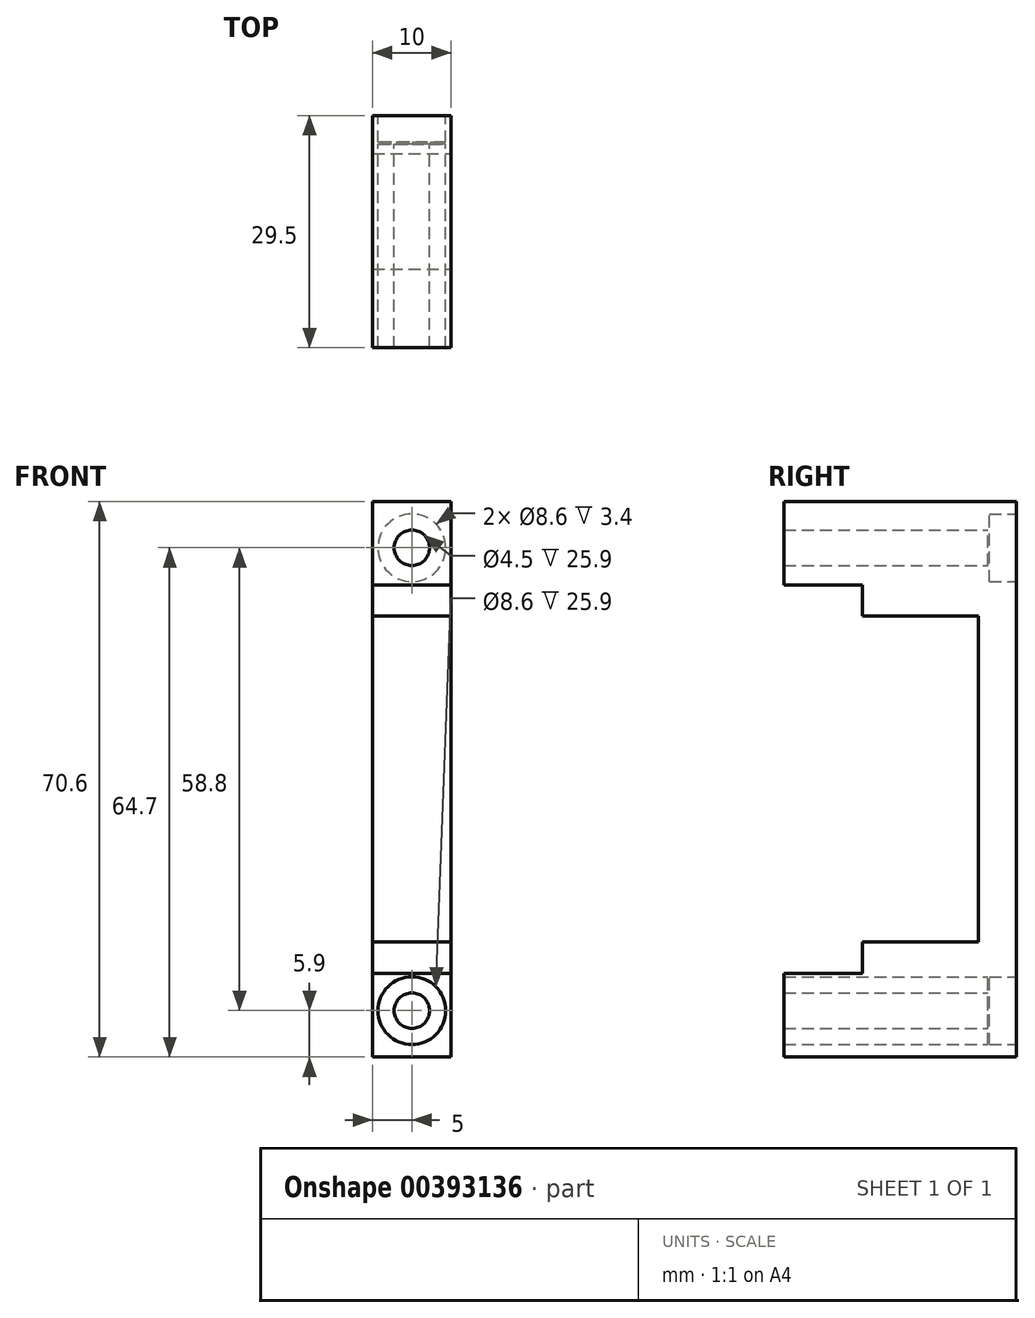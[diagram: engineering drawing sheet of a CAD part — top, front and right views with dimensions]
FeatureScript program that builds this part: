
annotation { "Feature Type Name" : "Feature", "Feature Type Description" : "" }
export const myFeature = defineFeature(function(context is Context, id is Id, definition is map)
    precondition{}
    {
        {
            var Q0;
            Q0=qCreatedBy(makeId("Front.planeOp"),FACE);
            var sketch = newSketch(context, id + "F0", { "sketchPlane" : qUnion([Q0])});
            skLineSegment(sketch, "E0", {"start": v(5, 35.3) * mm, "end": v(-5, 35.3) * mm});
            skPoint(sketch, "E1", {"position": v(0, 35.3) * mm});
            skLineSegment(sketch, "E2.MirrorCS", {"start": v(5, -35.3) * mm, "end": v(-5, -35.3) * mm});
            skPoint(sketch, "E3.MirrorP", {"position": v(0, -35.3) * mm});
            skLineSegment(sketch, "E4", {"start": v(-5, 35.3) * mm, "end": v(-5, -35.3) * mm});
            skLineSegment(sketch, "E5", {"start": v(5, -35.3) * mm, "end": v(5, 35.3) * mm});
            skLineSegment(sketch, "E6", {"start": v(-5, 24.7) * mm, "end": v(5, 24.7) * mm});
            skLineSegment(sketch, "E7", {"start": v(-5, 20.7) * mm, "end": v(5, 20.7) * mm});
            skLineSegment(sketch, "E8.MirrorCS", {"start": v(-5, -24.7) * mm, "end": v(5, -24.7) * mm});
            skLineSegment(sketch, "E9.MirrorCS", {"start": v(-5, -20.7) * mm, "end": v(5, -20.7) * mm});
            skCircle(sketch, "E10", {"center": v(0, 29.4) * mm, "radius": 2.25 * mm});
            skCircle(sketch, "E11", {"center": v(0, 29.4) * mm, "radius": 4.3 * mm});
            skCircle(sketch, "E12.MirrorC", {"center": v(0, -29.4) * mm, "radius": 2.25 * mm});
            skCircle(sketch, "E13.MirrorC", {"center": v(0, -29.4) * mm, "radius": 4.3 * mm});
            skSolve(sketch);
        }
        {
            var Q0;
            {var subQ0=sQuery(id+"F0.wireOp",EDGE,"E7");Q0=makeQuery(id+"F0.imprint","IMPRINT",FACE,{"disambiguationData":[TD([[makeQuery(id+"F0.imprint","IMPRINT",EDGE,{"derivedFrom":subQ0}),-1.0]])]});}
            extrude(context, id + "F1", {"entities" : qUnion([Q0]), "depth" : 4.8 * mm});
        }
        {
            var Q0;
            {var subQ0=sQuery(id+"F0.wireOp",EDGE,"E6");Q0=makeQuery(id+"F0.imprint","IMPRINT",FACE,{"disambiguationData":[TD([[makeQuery(id+"F0.imprint","IMPRINT",EDGE,{"derivedFrom":subQ0}),-1.0]])]});}
            var Q1;
            {var subQ0=sQuery(id+"F0.wireOp",EDGE,"E8.MirrorCS");Q1=makeQuery(id+"F0.imprint","IMPRINT",FACE,{"disambiguationData":[TD([[makeQuery(id+"F0.imprint","IMPRINT",EDGE,{"derivedFrom":subQ0}),1.0]])]});}
            extrude(context, id + "F2", {"entities" : qUnion([Q0, Q1]), "operationType" : NewBodyOperationType.ADD, "depth" : 19.5 * mm});
        }
        {
            var Q0;
            {var subQ1=sQuery(id+"F0.wireOp",EDGE,"E0");Q0=makeQuery(id+"F0.imprint","IMPRINT",FACE,{"disambiguationData":[TD([[makeQuery(id+"F0.imprint","IMPRINT",EDGE,{"derivedFrom":subQ1}),1.0]])]});}
            var Q1;
            Q1=makeQuery(id+"F0.imprint","IMPRINT",FACE,{"disambiguationData":[TD([[makeQuery(id+"F0.imprint","IMPRINT",EDGE,{"derivedFrom":sQuery(id+"F0.wireOp",EDGE,"E10")}),-1.0]])]});
            var Q2;
            {var subQ2=sQuery(id+"F0.wireOp",EDGE,"E2.MirrorCS");Q2=makeQuery(id+"F0.imprint","IMPRINT",FACE,{"disambiguationData":[TD([[makeQuery(id+"F0.imprint","IMPRINT",EDGE,{"derivedFrom":subQ2}),-1.0]])]});}
            var Q3;
            Q3=makeQuery(id+"F0.imprint","IMPRINT",FACE,{"disambiguationData":[TD([[makeQuery(id+"F0.imprint","IMPRINT",EDGE,{"derivedFrom":sQuery(id+"F0.wireOp",EDGE,"E12.MirrorC")}),1.0]])]});
            extrude(context, id + "F3", {"entities" : qUnion([Q0, Q1, Q2, Q3]), "operationType" : NewBodyOperationType.ADD, "depth" : 29.5 * mm});
        }
        {
            var Q0;
            Q0=makeQuery(id+"F0.imprint","IMPRINT",FACE,{"disambiguationData":[TD([[makeQuery(id+"F0.imprint","IMPRINT",EDGE,{"derivedFrom":sQuery(id+"F0.wireOp",EDGE,"E12.MirrorC")}),1.0]])]});
            var Q1;
            Q1=makeQuery(id+"F0.imprint","IMPRINT",FACE,{"disambiguationData":[TD([[makeQuery(id+"F0.imprint","IMPRINT",EDGE,{"derivedFrom":sQuery(id+"F0.wireOp",EDGE,"E10")}),-1.0]])]});
            extrude(context, id + "F4", {"entities" : qUnion([Q0, Q1]), "operationType" : NewBodyOperationType.REMOVE, "depth" : 3.4 * mm});
        }
        {
            var Q0;
            Q0=makeQuery(id+"F0.imprint","IMPRINT",FACE,{"disambiguationData":[TD([[makeQuery(id+"F0.imprint","IMPRINT",EDGE,{"derivedFrom":sQuery(id+"F0.wireOp",EDGE,"E10")}),1.0]])]});
            var Q1;
            Q1=makeQuery(id+"F0.imprint","IMPRINT",FACE,{"disambiguationData":[TD([[makeQuery(id+"F0.imprint","IMPRINT",EDGE,{"derivedFrom":sQuery(id+"F0.wireOp",EDGE,"E12.MirrorC")}),-1.0]])]});
            extrude(context, id + "F5", {"entities" : qUnion([Q0, Q1]), "operationType" : NewBodyOperationType.ADD, "depth" : 3.6 * mm});
        }
        {
            var Q0;
            Q0=makeQuery(id+"F0.imprint","IMPRINT",FACE,{"disambiguationData":[TD([[makeQuery(id+"F0.imprint","IMPRINT",EDGE,{"derivedFrom":sQuery(id+"F0.wireOp",EDGE,"E12.MirrorC")}),-1.0]])]});
            var Q1;
            Q1=makeQuery(id+"F0.imprint","IMPRINT",FACE,{"disambiguationData":[TD([[makeQuery(id+"F0.imprint","IMPRINT",EDGE,{"derivedFrom":sQuery(id+"F0.wireOp",EDGE,"E10")}),1.0]])]});
            extrude(context, id + "F6", {"entities" : qUnion([Q0, Q1]), "operationType" : NewBodyOperationType.REMOVE, "depth" : 3.4 * mm});
        }
    });
